# Revit family: Haworth_CabanaLounge_Half-BackSofa_Retreat_EU_PRELIMINARY
name_source: partatom
category: Furniture
revit_build: Autodesk Revit 2018 (Build: 20170223_1515(x64)
units: mm (PartAtom-declared; Revit-internal decimal feet)

## family parameters
Always vertical = Yes
Cut with Voids When Loaded = No
OmniClass Number = 23.40.70.14.64.21
OmniClass Title = Systems Furniture
Room Calculation Point = No
Shared = No
Work Plane-Based = No

## types (8) — shared parameters
Actual Depth = 81 cm
Actual Width = 264 cm
Assembly Code = E2020200
Back Width = 107 cm
Description = Haworth - Cabana Lounge - Half Back Sofa - Retreat
Leg Offset = 7 cm
Manufacturer = Haworth
Model = SECBFR
Rectangle Control = No
Revision Number = 1
Screen Width = 188 cm
Seat Depth = 76 cm
Seat Height = 46 cm
Seat Width = 183 cm
Size = Verify Final Dim. w/ Haworth
Square Control = Yes
Table Width = 76 cm
URL = https://www.haworth.com
URL - Product = https://www.haworth.com
Warranty = http://www.haworth.com

## per-type parameters (varying)
| type | Actual Height | High Screen | Low Screen | Tiered Top | With Top |
| High Screen - With Integrated Table - With Tiered Top | 137 cm | Yes | No | Yes | Yes |
| High Screen - With Integrated Table - Without Tiered Top | 137 cm | Yes | No | No | Yes |
| High Screen - Without Integrated Table - Without Tiered Top | 137 cm | Yes | No | No | No |
| Low Screen - With Integrated Table - With Tiered Top | 107 cm | No | Yes | Yes | Yes |
| Low Screen - With Integrated Table - Without Tiered Top | 107 cm | No | Yes | No | Yes |
| Low Screen - Without Integrated Table - Without Tiered Top | 107 cm | No | Yes | No | No |
| High Screen - Without Integrated Table - With Tiered Top | 137 cm | Yes | No | Yes | No |
| Low Screen - Without Integrated Table - With Tiered Top | 107 cm | No | Yes | Yes | No |

## geometry (parser evidence)
native form markers: Extrusion x6, Sweep x18
no freeform markers — native parametric forms only
